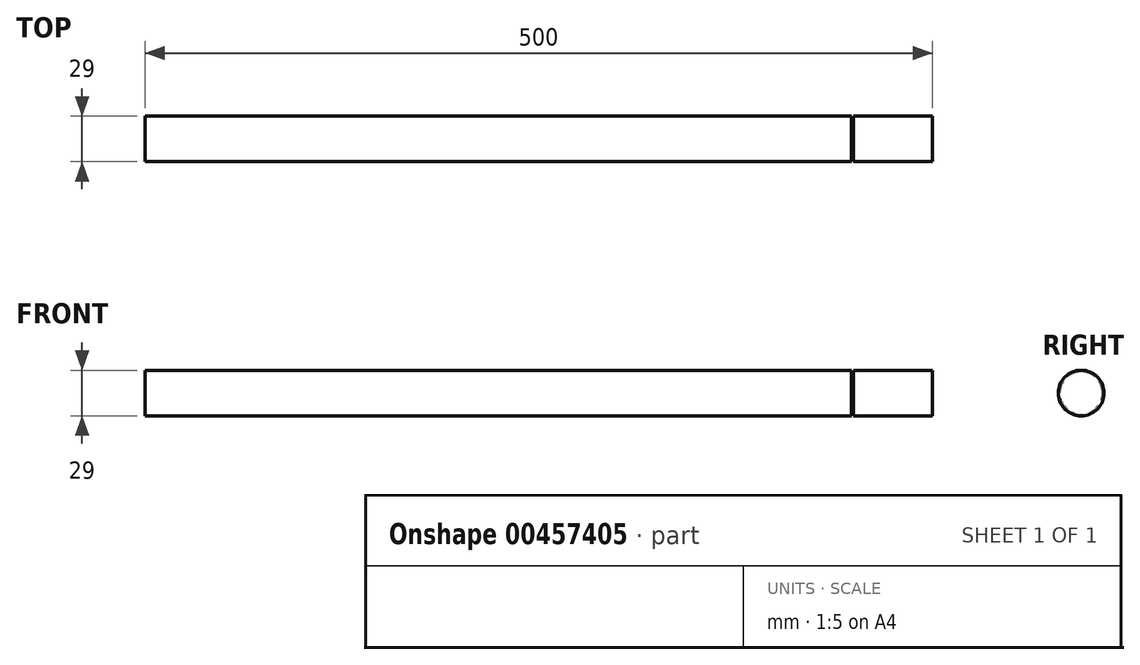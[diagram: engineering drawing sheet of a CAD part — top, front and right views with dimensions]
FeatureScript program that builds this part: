
annotation { "Feature Type Name" : "Feature", "Feature Type Description" : "" }
export const myFeature = defineFeature(function(context is Context, id is Id, definition is map)
    precondition{}
    {
        {
            var Q0;
            Q0=qCreatedBy(makeId("Front.planeOp"),FACE);
            var sketch = newSketch(context, id + "F0", { "sketchPlane" : qUnion([Q0])});
            skLineSegment(sketch, "E0", {"start": v(-250, 0) * mm, "end": v(250, 0) * mm});
            skLineSegment(sketch, "E1", {"start": v(250, 0) * mm, "end": v(250, 14.5) * mm});
            skLineSegment(sketch, "E2", {"start": v(250, 14.5) * mm, "end": v(200, 14.5) * mm});
            skLineSegment(sketch, "E3", {"start": v(200, 14.5) * mm, "end": v(200, 14.5) * mm});
            skLineSegment(sketch, "E4", {"start": v(198.5, 14.5) * mm, "end": v(198.5, 14.5) * mm});
            skLineSegment(sketch, "E5", {"start": v(198.5, 14.5) * mm, "end": v(-250, 14.5) * mm});
            skLineSegment(sketch, "E6", {"start": v(-250, 14.5) * mm, "end": v(-250, 0) * mm});
            skLineSegment(sketch, "E7", {"start": v(198.5, 14.5) * mm, "end": v(198.5, 13.5) * mm});
            skLineSegment(sketch, "E8", {"start": v(200, 13.5) * mm, "end": v(200, 14.5) * mm});
            skLineSegment(sketch, "E9", {"start": v(200, 13.5) * mm, "end": v(198.5, 13.5) * mm});
            skSolve(sketch);
        }
        {
            var Q0;
            Q0 = qSketchRegion(id + "F0", true);
            var Q1;
            Q1=sQuery(id+"F0.wireOp",EDGE,"E0");
            revolve(context, id + "F1", {"entities" : qUnion([Q0]), "axis" : qUnion([Q1]), "revolveType" : RevolveType.FULL});
        }
    });
